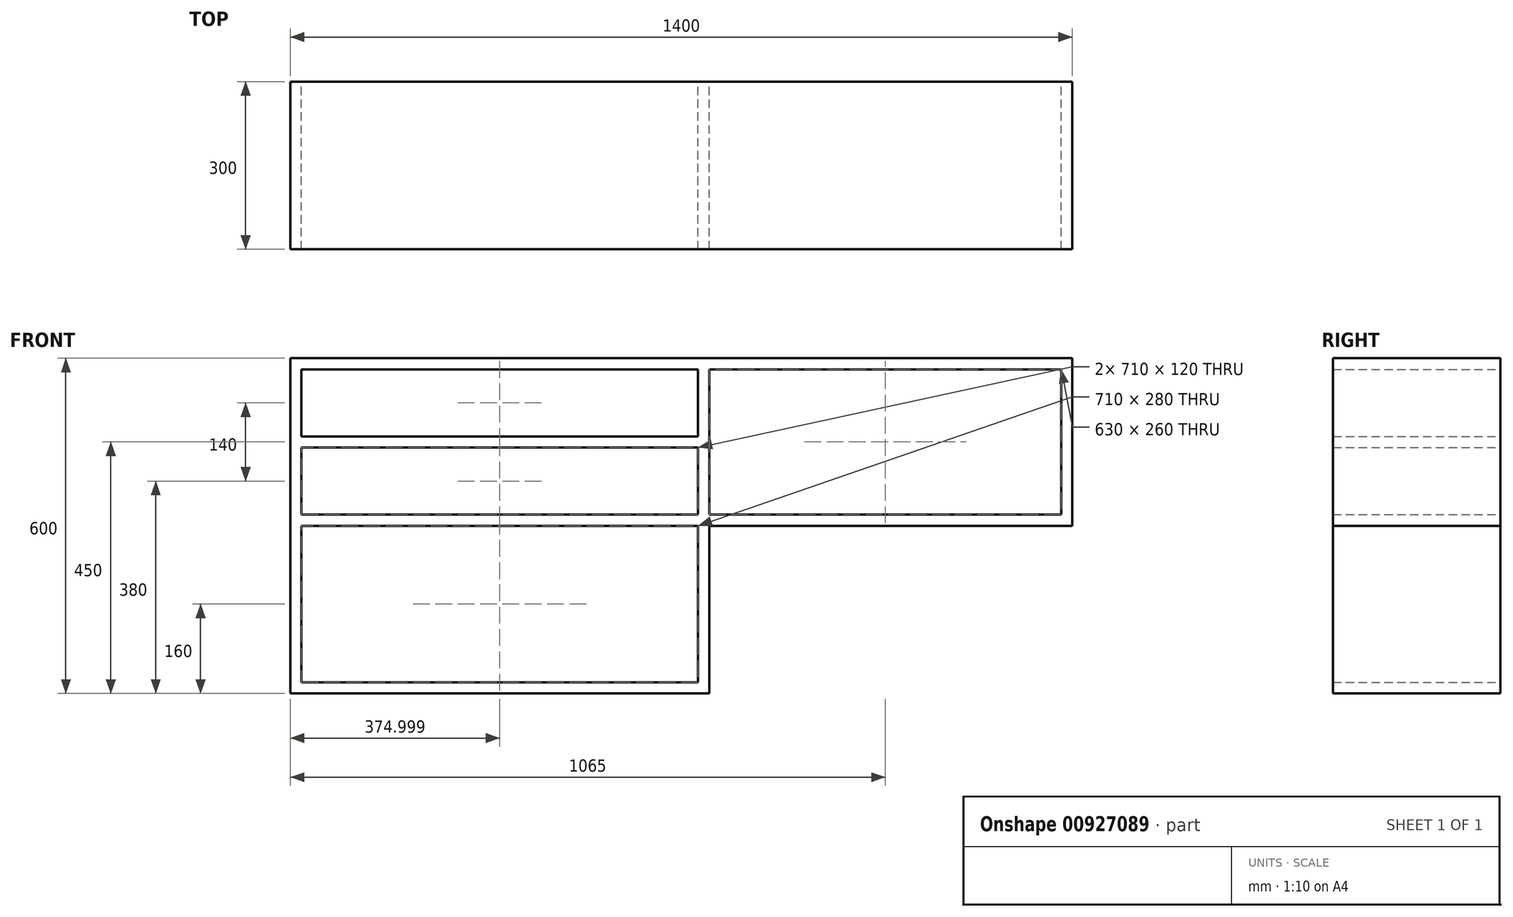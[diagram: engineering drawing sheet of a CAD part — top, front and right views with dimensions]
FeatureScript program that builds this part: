
annotation { "Feature Type Name" : "Feature", "Feature Type Description" : "" }
export const myFeature = defineFeature(function(context is Context, id is Id, definition is map)
    precondition{}
    {
        {
            var Q0;
            Q0=qCreatedBy(makeId("Front.planeOp"),FACE);
            var sketch = newSketch(context, id + "F0", { "sketchPlane" : qUnion([Q0])});
            skLineSegment(sketch, "E0", {"start": v(-49.43, 0) * mm, "end": v(700.57, 0) * mm});
            skLineSegment(sketch, "E1", {"start": v(-49.43, 0) * mm, "end": v(-49.43, 600) * mm});
            skLineSegment(sketch, "E2", {"start": v(-49.43, 600) * mm, "end": v(1350.57, 600) * mm});
            skLineSegment(sketch, "E3", {"start": v(700.57, 0) * mm, "end": v(700.57, 300) * mm});
            skLineSegment(sketch, "E4", {"start": v(700.57, 300) * mm, "end": v(1350.57, 300) * mm});
            skLineSegment(sketch, "E5", {"start": v(1350.57, 300) * mm, "end": v(1350.57, 600) * mm});
            skLineSegment(sketch, "E6.0", {"start": v(-49.43, 580) * mm, "end": v(1350.57, 580) * mm});
            skLineSegment(sketch, "E7.0", {"start": v(1330.57, 300) * mm, "end": v(1330.57, 600) * mm});
            skLineSegment(sketch, "E8.0", {"start": v(700.57, 320) * mm, "end": v(1350.57, 320) * mm});
            skLineSegment(sketch, "E9.0", {"start": v(680.57, 0) * mm, "end": v(680.57, 300) * mm});
            skLineSegment(sketch, "E10.0", {"start": v(-49.43, 20) * mm, "end": v(700.57, 20) * mm});
            skLineSegment(sketch, "E11.0", {"start": v(-29.43, 0) * mm, "end": v(-29.43, 600) * mm});
            skLineSegment(sketch, "E12", {"start": v(680.57, 300) * mm, "end": v(680.57, 320) * mm});
            skLineSegment(sketch, "E13", {"start": v(700.57, 320) * mm, "end": v(680.57, 320) * mm});
            skLineSegment(sketch, "E14", {"start": v(680.57, 300) * mm, "end": v(-29.43, 300) * mm});
            skLineSegment(sketch, "E15", {"start": v(680.57, 320) * mm, "end": v(-29.43, 320) * mm});
            skLineSegment(sketch, "E16", {"start": v(680.57, 320) * mm, "end": v(680.57, 580) * mm});
            skLineSegment(sketch, "E17", {"start": v(700.57, 320) * mm, "end": v(700.57, 580) * mm});
            skLineSegment(sketch, "E18.0", {"start": v(680.57, 460) * mm, "end": v(-29.43, 460) * mm});
            skLineSegment(sketch, "E19.0", {"start": v(680.57, 440) * mm, "end": v(-29.43, 440) * mm});
            skPoint(sketch, "E20.start.orphan", {"position": v(680.57, 450) * mm});
            skSolve(sketch);
        }
        {
            var Q0;
            Q0 = qSketchRegion(id + "F0", true);
            var Q1;
            {var subQ0=sQuery(id+"F0.wireOp",EDGE,"E18.0");Q1=makeQuery(id+"F0.imprint","IMPRINT",FACE,{"disambiguationData":[TD([[makeQuery(id+"F0.imprint","IMPRINT",EDGE,{"derivedFrom":subQ0}),1.0]])]});}
            var Q2;
            {var subQ1=sQuery(id+"F0.wireOp",EDGE,"E13");Q2=makeQuery(id+"F0.imprint","IMPRINT",FACE,{"disambiguationData":[TD([[makeQuery(id+"F0.imprint","IMPRINT",EDGE,{"derivedFrom":subQ1}),-1.0]])]});}
            var Q3;
            Q3=makeQuery(id+"F0.imprint","IMPRINT",FACE,{"disambiguationData":[TD([[makeQuery(id+"F0.imprint","IMPRINT",EDGE,{"derivedFrom":sQuery(id+"F0.wireOp",EDGE,"E12")}),1.0]])]});
            extrude(context, id + "F1", {"entities" : qUnion([Q0, Q1, Q2, Q3]), "depth" : 300 * mm, "offsetDistance" : 25 * mm});
        }
    });
